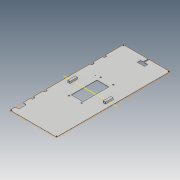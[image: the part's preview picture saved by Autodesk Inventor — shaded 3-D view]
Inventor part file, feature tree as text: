
AUTODESK INVENTOR PART (.ipt)
format: ipt  version: 2019 (Build 230136000, 136)  size: 273,920 bytes
history: native  units: mm
features: sketch x9, extrude x5, hole x3, fillet x2, plane x1
ambient origin geometry x8: Origin, YZ Plane, XZ Plane, XY Plane, X Axis, Y Axis, Z Axis, Center Point
bodies: Solid1 (feature_tree)
feature tree (20):
  sketch  "Sketch1"  dims[d3=1.0mm d6=1.0mm d7=0.0mm]
  extrude  "Extrusion1"  Depth=1.0mm TaperAngle=0.0deg
  plane  "Work Plane1"
  extrude  "Extrusion2"  Depth=20.0mm
  hole  "Hole1"  [1 undecoded]
  hole  "Hole2"  [1 undecoded]
  hole  "Hole3"  [1 undecoded]
  extrude  "Extrusion3"  Depth=3.0mm
  fillet  "Fillet1"  Radius=3.0mm
  extrude  "Extrusion4"  Depth=69.0mm
  extrude  "Extrusion5"  Depth=32.0mm
  fillet  "Fillet2"  Radius=34.5mm
  sketch  "Sketch2"  dims[d10=6.0mm d11=20.0mm]
  sketch  "Sketch4"  dims[d12=10.0mm d13=6.0mm]
  sketch  "Sketch6"  dims[d14=20.0mm d15=10.0mm]
  sketch  "Sketch7"  dims[d16=5.0mm d17=0.0mm d22=2.5mm]
  sketch  "Sketch8"  dims[d23=3.0mm d24=2.5mm d25=3.0mm]
  sketch  "Sketch9"  dims[d26=2.6mm d27=6.0mm d28=5.0mm d29=2.0mm d30=14.3117mm d31=5.0mm d32=0.0mm]
  sketch  "Sketch10"  dims[d33=2.6mm d34=6.0mm d35=5.0mm d36=2.0mm d37=14.3117mm d38=15.0mm d39=20.594885mm]
  sketch  "Sketch11"  dims[d40=2.6mm d41=6.0mm d42=5.0mm d43=2.0mm d44=14.3117mm d45=15.0mm d46=20.594885mm d47=69.0mm d48=32.0mm d52=34.5mm d53=16.0mm d54=3.5mm d55=3.5mm d56=3.5mm d57=3.5mm d59=0.0mm d62=0.0mm d64=0.0mm d65=0.0mm d66=11.0mm d67=4.8mm d68=1.0mm d69=1.0mm d70=55.0mm d71=7.0mm d72=7.0mm d73=26.0mm d74=26.0mm d75=7.0mm d76=7.0mm d77=119.0mm d78=4.5mm d79=4.5mm d80=1.0mm d81=1.0mm d82=5.0mm d83=0.0mm d84=2.0mm d85=0.0mm d86=0.0mm d87=2.0mm d88=2.0mm d89=2.0mm d90=2.0mm d91=2.0mm d92=2.0mm d93=2.0mm d94=2.0mm d95=2.0mm d96=2.0mm d97=2.0mm d98=2.0mm d99=10.0mm d100=0.0mm d101=3.0mm]
note: 3 required parameter values undecoded (feature->parameter linkage not recoverable at this tier; creation-order binding heuristic only, values carry confidence <= 0.55)
